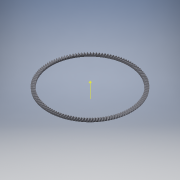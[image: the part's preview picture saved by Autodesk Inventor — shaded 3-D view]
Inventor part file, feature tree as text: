
AUTODESK INVENTOR PART (.ipt)
format: ipt  version: 2016 (Build 200138000, 138)  size: 2,597,376 bytes
history: native  units: mm
features: other x24, loft x2, pattern_circular x2, sketch x2, extrude x1
ambient origin geometry x6: Origin, XZ Plane, X Axis, Y Axis, Z Axis, Center Point
bodies: Solid1 (feature_tree)
feature tree (31):
  other  "Top Point"
  other  "Mesh Plane2"
  other  "Teeth Body"
  other  "Start Point"
  other  "Tooth Plane"
  other  "Start Sketch"
  other  "End Point"
  other  "3D Sketch Right"
  other  "End Plane Right"
  loft  "Loft Right"
  pattern_circular  "Circular Pattern Right"  [2 undecoded]
  other  "3D Sketch Left"
  other  "End Plane Left"
  loft  "Loft Left"
  pattern_circular  "Circular Pattern Left"  Angle=90.0deg  [1 undecoded]
  other  "Fix Body"
  extrude  "Extrusion1"  Depth=10.0mm
  other  "Mesh Plane"
  other  "Top Plane"
  other  "Teeth Body Sketch"
  other  "End Plane"
  other  "End Sketch"
  other  "Helical Curve Left"
  other  "End Sketch Left"
  other  "Body Sketch"
  sketch  "Sketch6"  dims[d0=317.5mm d1=316.917462mm]
  other  "Srf1"
  other  "Helical Curve Right"
  other  "End Sketch Right"
  sketch  "Sketch8"  dims[d2=317.985448mm d3=12.7mm d4=12.711624mm d5=90.0deg d7=809.750702mm d8=718.43191mm d9=1283.869065mm d11=12.9794mm d12=744.658217mm d15=660.680162mm d16=1180.664179mm d17=0.0mm d18=90.0deg d19=0.0mm d20=90.0deg d21=1250.0mm d22=360.0deg d26=341.565782mm d27=1.24032mm d28=317.5mm d29=-14.750896mm d30=744.658217mm d31=660.680162mm d32=1180.664179mm d35=0.0mm d37=0.0mm d39=0.0mm d40=90.0deg d41=1250.0mm d42=360.0deg d46=90.0deg d47=90.0deg d48=0.0mm d49=0.0mm d50=90.0deg d51=0.251327mm d52=0.0mm d53=0.0mm d54=0.0mm d56=14.07707mm d57=1665.464758mm d58=1657.529798mm d59=1531.584984mm d60=1524.287883mm d61=1531.584984mm d62=1524.287883mm d63=90.0deg d64=90.0deg d65=341.565782mm d66=31.5mm d67=317.5mm d68=-14.750896mm d69=1.24032mm d70=660.680162mm d71=1180.664179mm d72=744.658217mm d73=1524.287883mm d74=1531.584984mm d75=0.0mm d76=90.0deg d77=0.0mm d78=90.0deg d79=0.0mm d80=90.0deg d81=1250.0mm d82=360.0deg d84=10.0mm d85=20.0mm d86=20.0mm d87=10.0mm d88=0.0mm d89=0.0mm d90=25.4mm d91=0.0mm]
  other  "Pitch Diameter"
note: 3 required parameter values undecoded (feature->parameter linkage not recoverable at this tier; creation-order binding heuristic only, values carry confidence <= 0.55)
